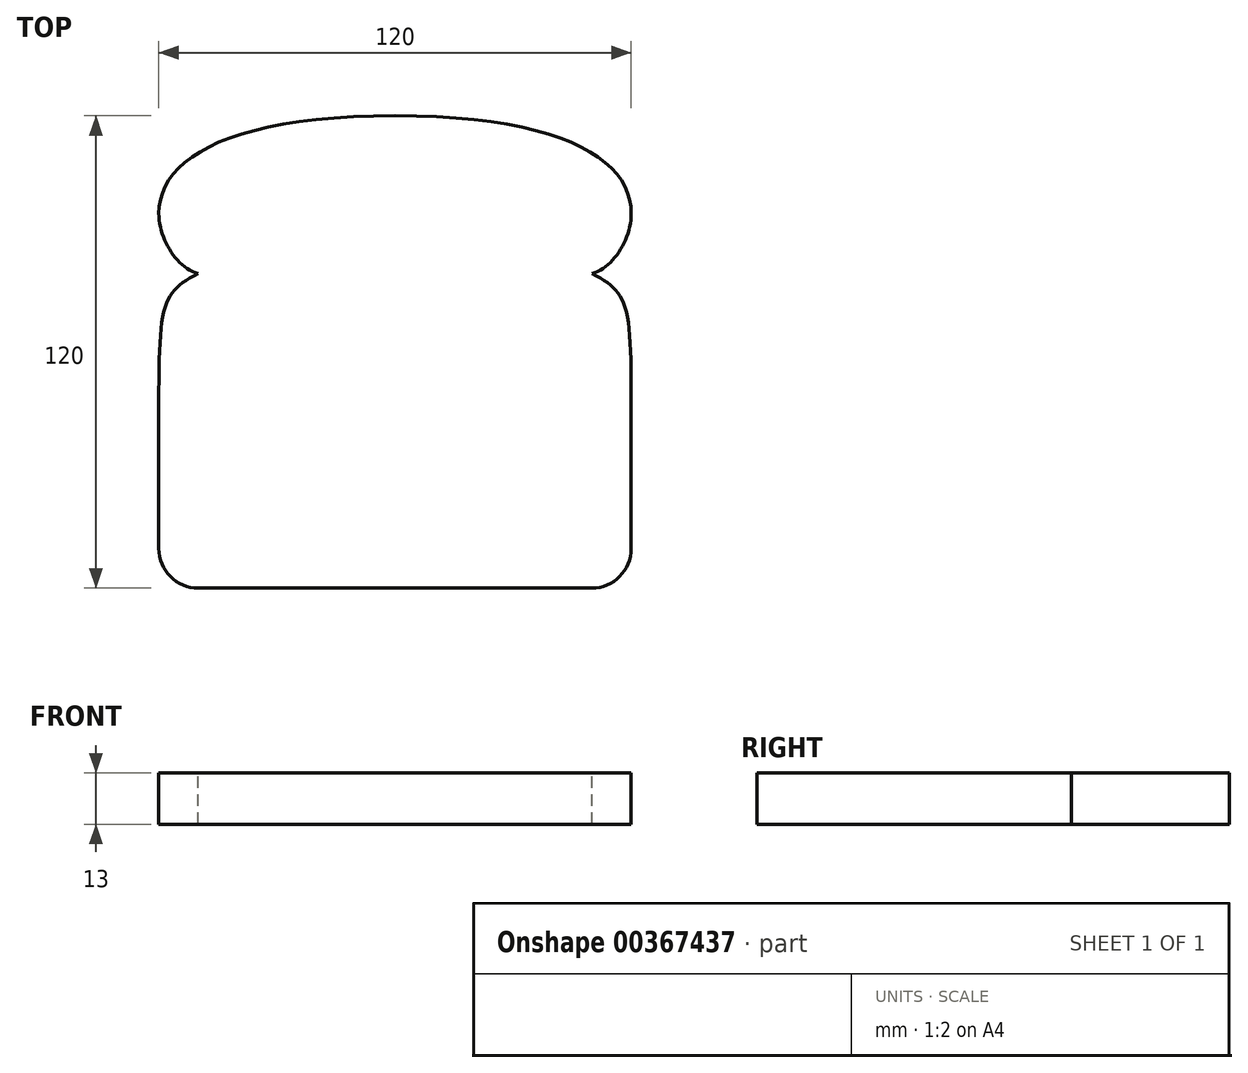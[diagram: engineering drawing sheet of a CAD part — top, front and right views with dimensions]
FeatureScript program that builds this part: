
annotation { "Feature Type Name" : "Feature", "Feature Type Description" : "" }
export const myFeature = defineFeature(function(context is Context, id is Id, definition is map)
    precondition{}
    {
        {
            var Q0;
            Q0=qCreatedBy(makeId("Top.planeOp"),FACE);
            var sketch = newSketch(context, id + "F0", { "sketchPlane" : qUnion([Q0])});
            skLineSegment(sketch, "E0", {"start": v(0, 81.07) * mm, "end": v(-60, 81.07) * mm});
            skLineSegment(sketch, "E1", {"start": v(-60, 81.07) * mm, "end": v(-60, -38.93) * mm});
            skLineSegment(sketch, "E2", {"start": v(-60, -38.93) * mm, "end": v(0, -38.93) * mm});
            skLineSegment(sketch, "E3.MirrorCS", {"start": v(60, -38.93) * mm, "end": v(0, -38.93) * mm});
            skLineSegment(sketch, "E4.MirrorCS", {"start": v(0, 81.07) * mm, "end": v(60, 81.07) * mm});
            skLineSegment(sketch, "E5.MirrorCS", {"start": v(60, 81.07) * mm, "end": v(60, -38.93) * mm});
            skSolve(sketch);
        }
        {
            var Q0;
            Q0=makeQuery(id+"F0.imprint","IMPRINT",FACE,{"disambiguationData":[TD([[makeQuery(id+"F0.imprint","IMPRINT",EDGE,{"derivedFrom":sQuery(id+"F0.wireOp",EDGE,"E0")}),1.0]])]});
            extrude(context, id + "F1", {"entities" : qUnion([Q0]), "depth" : 13 * mm});
        }
        {
            var Q0;
            Q0=makeQuery(id+"F1.opExtrude","CAP_FACE",FACE,{"disambiguationData":[OSD([sQuery(id+"F0.wireOp",EDGE,"E0"),sQuery(id+"F0.wireOp",EDGE,"E1"),sQuery(id+"F0.wireOp",EDGE,"E2"),sQuery(id+"F0.wireOp",EDGE,"E3.MirrorCS"),sQuery(id+"F0.wireOp",EDGE,"E4.MirrorCS"),sQuery(id+"F0.wireOp",EDGE,"E5.MirrorCS")])],"isStart":false});
            var sketch = newSketch(context, id + "F2", { "sketchPlane" : qUnion([Q0])});
            skFitSpline(sketch, "E6", {"points": [v(0, 81.07) * mm, v(-60, 56.24) * mm], "startDerivative": vector(-128.4, 0) * mm, "endDerivative": vector(0, -40.61) * mm});
            skFitSpline(sketch, "E7", {"points": [v(-60, 56.24) * mm, v(-50.07, 40.95) * mm], "startDerivative": vector(0, -19.56) * mm, "endDerivative": vector(16.38, -5.02) * mm});
            skFitSpline(sketch, "E8", {"points": [v(-50.07, 40.95) * mm, v(-60, 11.07) * mm], "startDerivative": vector(-25.68, -13.94) * mm, "endDerivative": vector(0, -69.08) * mm});
            skLineSegment(sketch, "E9", {"start": v(-60, 11.07) * mm, "end": v(-60, -28.93) * mm});
            skLineSegment(sketch, "E10", {"start": v(-50, -38.93) * mm, "end": v(0, -38.93) * mm});
            skPoint(sketch, "E11.visualSharp", {"position": v(-60, -38.93) * mm});
            skArc(sketch, "E11.filletArc", {"start": v(-60, -28.93) * mm, "mid": v(-57.07, -36) * mm, "end": v(-50, -38.93) * mm});
            skLineSegment(sketch, "E12", {"start": v(0, -38.93) * mm, "end": v(0, -77.2) * mm});
            skLineSegment(sketch, "E13", {"start": v(0, -77.2) * mm, "end": v(-101.8, -77.2) * mm});
            skLineSegment(sketch, "E14", {"start": v(-101.8, -77.2) * mm, "end": v(-101.8, 81.07) * mm});
            skLineSegment(sketch, "E15", {"start": v(0, 81.07) * mm, "end": v(0, 81.07) * mm});
            skArc(sketch, "E16.MirrorCS", {"start": v(60, -28.93) * mm, "mid": v(57.07, -36) * mm, "end": v(50, -38.93) * mm});
            skFitSpline(sketch, "E17.MirrorCS", {"points": [v(60, 56.24) * mm, v(50.07, 40.95) * mm], "startDerivative": vector(0, -19.56) * mm, "endDerivative": vector(-16.38, -5.02) * mm});
            skLineSegment(sketch, "E18.MirrorCS", {"start": v(0, -77.2) * mm, "end": v(101.8, -77.2) * mm});
            skLineSegment(sketch, "E19.MirrorCS", {"start": v(50, -38.93) * mm, "end": v(0, -38.93) * mm});
            skFitSpline(sketch, "E20.MirrorCS", {"points": [v(0, 81.07) * mm, v(60, 56.24) * mm], "startDerivative": vector(128.4, 0) * mm, "endDerivative": vector(0, -40.61) * mm});
            skLineSegment(sketch, "E21.MirrorCS", {"start": v(101.8, -77.2) * mm, "end": v(101.8, 81.07) * mm});
            skLineSegment(sketch, "E22.MirrorCS", {"start": v(60, 11.07) * mm, "end": v(60, -28.93) * mm});
            skPoint(sketch, "E23.MirrorP", {"position": v(60, -38.93) * mm});
            skFitSpline(sketch, "E24.MirrorCS", {"points": [v(50.07, 40.95) * mm, v(60, 11.07) * mm], "startDerivative": vector(25.68, -13.94) * mm, "endDerivative": vector(0, -69.08) * mm});
            skLineSegment(sketch, "E25", {"start": v(-101.8, 81.07) * mm, "end": v(-101.8, 114.12) * mm});
            skLineSegment(sketch, "E26", {"start": v(-101.8, 114.12) * mm, "end": v(101.8, 114.12) * mm});
            skLineSegment(sketch, "E27", {"start": v(101.8, 114.12) * mm, "end": v(101.8, 81.07) * mm});
            skSolve(sketch);
        }
        {
            var Q0;
            Q0=qSketchRegion(id+"F2",true);
            extrude(context, id + "F3", {"entities" : qUnion([Q0]), "operationType" : NewBodyOperationType.REMOVE, "oppositeDirection" : true, "depth" : 25 * mm});
        }
    });
